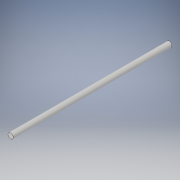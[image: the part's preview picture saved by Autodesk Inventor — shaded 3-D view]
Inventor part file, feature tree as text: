
AUTODESK INVENTOR PART (.ipt)
format: ipt  version: 2018 (Build 220112000, 112)  size: 89,600 bytes
history: native  units: mm
features: extrude x1, sketch x1
ambient origin geometry x8: Origin, YZ Plane, XZ Plane, XY Plane, X Axis, Y Axis, Z Axis, Center Point
bodies: Volumenkörper1 (feature_tree)
feature tree (2):
  extrude  "Extrusion1"  Depth=150.0mm TaperAngle=0.0deg
  sketch  "Skizze1"  dims[d0=5.0mm d1=150.0mm d2=0.0mm]
